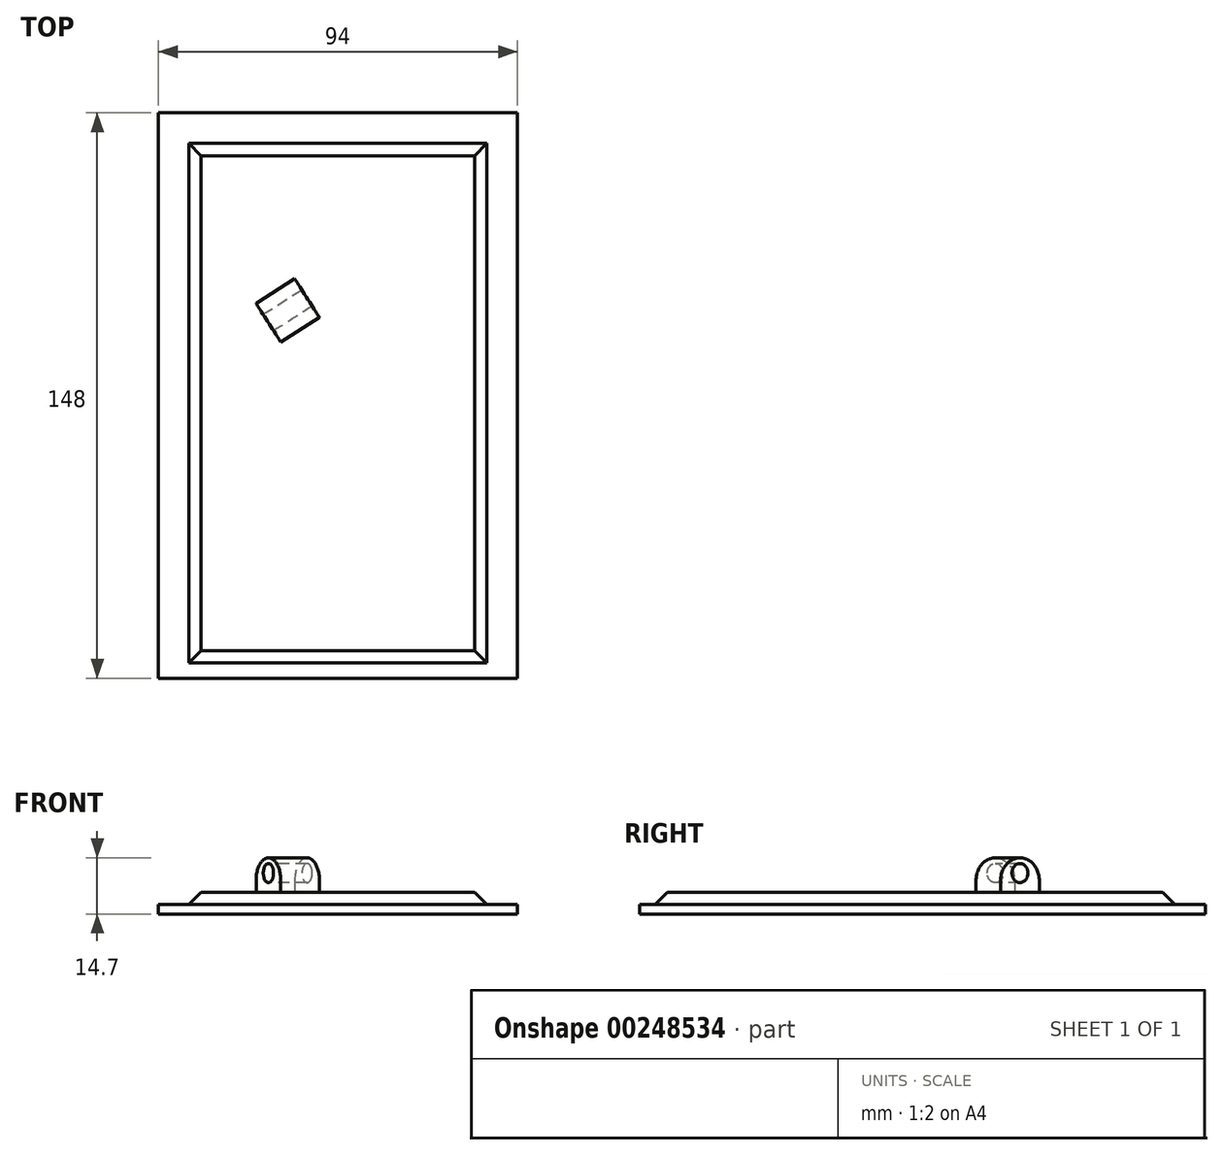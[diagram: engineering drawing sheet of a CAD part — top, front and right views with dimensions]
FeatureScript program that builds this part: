
annotation { "Feature Type Name" : "Feature", "Feature Type Description" : "" }
export const myFeature = defineFeature(function(context is Context, id is Id, definition is map)
    precondition{}
    {
        {
            var Q0;
            Q0=qCreatedBy(makeId("Top.planeOp"),FACE);
            var sketch = newSketch(context, id + "F0", { "sketchPlane" : qUnion([Q0])});
            skLineSegment(sketch, "E0.bottom", {"start": v(47, 74) * mm, "end": v(-47, 74) * mm});
            skLineSegment(sketch, "E0.top", {"start": v(47, -74) * mm, "end": v(-47, -74) * mm});
            skLineSegment(sketch, "E0.left", {"start": v(47, 74) * mm, "end": v(47, -74) * mm});
            skLineSegment(sketch, "E0.right", {"start": v(-47, 74) * mm, "end": v(-47, -74) * mm});
            skPoint(sketch, "E0.middle", {"position": v(0, 0) * mm});
            skLineSegment(sketch, "E1.left", {"start": v(47, -74) * mm, "end": v(47, 74) * mm});
            skLineSegment(sketch, "E1.right", {"start": v(-47, -74) * mm, "end": v(-47, 74) * mm});
            skLineSegment(sketch, "E2.bottom", {"start": v(-39, 66) * mm, "end": v(39, 66) * mm});
            skLineSegment(sketch, "E2.top", {"start": v(-39, -70) * mm, "end": v(39, -70) * mm});
            skLineSegment(sketch, "E2.left", {"start": v(-39, 66) * mm, "end": v(-39, -70) * mm});
            skLineSegment(sketch, "E2.right", {"start": v(39, 66) * mm, "end": v(39, -70) * mm});
            skSolve(sketch);
        }
        {
            var Q0;
            Q0=makeQuery(id+"F0.imprint","IMPRINT",FACE,{"disambiguationData":[TD([[makeQuery(id+"F0.imprint","IMPRINT",EDGE,{"derivedFrom":sQuery(id+"F0.wireOp",EDGE,"E0.bottom")}),-1.0]])]});
            var Q1;
            Q1=makeQuery(id+"F0.imprint","IMPRINT",FACE,{"disambiguationData":[TD([[makeQuery(id+"F0.imprint","IMPRINT",EDGE,{"derivedFrom":sQuery(id+"F0.wireOp",EDGE,"E0.bottom")}),1.0]])]});
            var Q2;
            Q2=makeQuery(id+"F0.imprint","IMPRINT",FACE,{"disambiguationData":[TD([[makeQuery(id+"F0.imprint","IMPRINT",EDGE,{"derivedFrom":sQuery(id+"F0.wireOp",EDGE,"E2.bottom")}),-1.0]])]});
            var Q3;
            Q3=makeQuery(id+"F0.imprint","IMPRINT",FACE,{"disambiguationData":[TD([[makeQuery(id+"F0.imprint","IMPRINT",EDGE,{"derivedFrom":sQuery(id+"F0.wireOp",EDGE,"E0.top")}),-1.0]])]});
            extrude(context, id + "F1", {"entities" : qUnion([Q0, Q1, Q2, Q3]), "oppositeDirection" : true, "depth" : 2.5 * mm});
        }
        {
            var Q0;
            Q0=makeQuery(id+"F0.imprint","IMPRINT",FACE,{"disambiguationData":[TD([[makeQuery(id+"F0.imprint","IMPRINT",EDGE,{"derivedFrom":sQuery(id+"F0.wireOp",EDGE,"E2.bottom")}),-1.0]])]});
            extrude(context, id + "F2", {"entities" : qUnion([Q0]), "operationType" : NewBodyOperationType.ADD, "depth" : 3.2 * mm});
        }
        {
            var Q0;
            Q0=makeQuery(id+"F2.opExtrude","CAP_EDGE",EDGE,{"disambiguationData":[OSD([sQuery(id+"F0.wireOp",EDGE,"E0.top")])],"isStart":false});
            var Q1;
            Q1=makeQuery(id+"F2.opExtrude","CAP_EDGE",EDGE,{"disambiguationData":[OSD([sQuery(id+"F0.wireOp",EDGE,"E0.right")])],"isStart":false});
            var Q2;
            Q2=makeQuery(id+"F2.opExtrude","CAP_EDGE",EDGE,{"disambiguationData":[OSD([sQuery(id+"F0.wireOp",EDGE,"E0.left")])],"isStart":false});
            var Q3;
            Q3=makeQuery(id+"F2.opExtrude","CAP_EDGE",EDGE,{"disambiguationData":[OSD([sQuery(id+"F0.wireOp",EDGE,"E0.bottom")])],"isStart":false});
            var Q4;
            Q4=makeQuery(id+"F2.opExtrude","CAP_EDGE",EDGE,{"disambiguationData":[OSD([sQuery(id+"F0.wireOp",EDGE,"E2.left")])],"isStart":false});
            var Q5;
            Q5=makeQuery(id+"F2.opExtrude","CAP_EDGE",EDGE,{"disambiguationData":[OSD([sQuery(id+"F0.wireOp",EDGE,"E2.top")])],"isStart":false});
            var Q6;
            Q6=makeQuery(id+"F2.opExtrude","CAP_EDGE",EDGE,{"disambiguationData":[OSD([sQuery(id+"F0.wireOp",EDGE,"E2.right")])],"isStart":false});
            var Q7;
            Q7=makeQuery(id+"F2.opExtrude","CAP_EDGE",EDGE,{"disambiguationData":[OSD([sQuery(id+"F0.wireOp",EDGE,"E2.bottom")])],"isStart":false});
            chamfer(context, id + "F3", {"entities" : qUnion([Q0, Q1, Q2, Q3, Q4, Q5, Q6, Q7]), "width" : 3.2 * mm, "tangentPropagation" : true});
        }
        {
            var Q0;
            Q0=makeQuery(id+"F2.opExtrude","CAP_FACE",FACE,{"disambiguationData":[OSD([sQuery(id+"F0.wireOp",EDGE,"E2.bottom"),sQuery(id+"F0.wireOp",EDGE,"E2.top"),sQuery(id+"F0.wireOp",EDGE,"E2.left"),sQuery(id+"F0.wireOp",EDGE,"E2.right")])],"isStart":false});
            var sketch = newSketch(context, id + "F4", { "sketchPlane" : qUnion([Q0])});
            skLineSegment(sketch, "E3.bottom", {"start": v(-43.3, 70.8) * mm, "end": v(42.3, 70.8) * mm, "construction": true});
            skLineSegment(sketch, "E3.top", {"start": v(-43.3, -67.2) * mm, "end": v(42.3, -67.2) * mm, "construction": true});
            skLineSegment(sketch, "E3.left", {"start": v(-43.3, 70.8) * mm, "end": v(-43.3, -67.2) * mm, "construction": true});
            skLineSegment(sketch, "E3.right", {"start": v(42.3, 70.8) * mm, "end": v(42.3, -67.2) * mm, "construction": true});
            skLineSegment(sketch, "E4", {"start": v(-0.5, 70.8) * mm, "end": v(-0.5, -67.2) * mm});
            skLineSegment(sketch, "E5", {"start": v(-43.3, 24.8) * mm, "end": v(42.3, 24.8) * mm, "construction": true});
            skLineSegment(sketch, "E6", {"start": v(-14.77, 83.2) * mm, "end": v(-14.77, -67.2) * mm, "construction": true});
            skPoint(sketch, "E7.0", {"position": v(-50.1, 77.6) * mm});
            skPoint(sketch, "E8.0", {"position": v(49.1, -74) * mm});
            skLineSegment(sketch, "E9.bottom", {"start": v(-50.1, 77.6) * mm, "end": v(49.1, 77.6) * mm, "construction": true});
            skLineSegment(sketch, "E9.top", {"start": v(-50.1, -74) * mm, "end": v(49.1, -74) * mm, "construction": true});
            skLineSegment(sketch, "E9.left", {"start": v(-50.1, 77.6) * mm, "end": v(-50.1, -74) * mm, "construction": true});
            skLineSegment(sketch, "E9.right", {"start": v(49.1, 77.6) * mm, "end": v(49.1, -74) * mm, "construction": true});
            skLineSegment(sketch, "E10.bottom", {"start": v(55.5, 81) * mm, "end": v(-56.5, 81) * mm, "construction": true});
            skLineSegment(sketch, "E10.top", {"start": v(55.5, -74) * mm, "end": v(-56.5, -74) * mm, "construction": true});
            skLineSegment(sketch, "E10.left", {"start": v(55.5, 81) * mm, "end": v(55.5, -74) * mm, "construction": true});
            skLineSegment(sketch, "E10.right", {"start": v(-56.5, 81) * mm, "end": v(-56.5, -74) * mm, "construction": true});
            skPoint(sketch, "E10.middle", {"position": v(-0.5, 3.5) * mm});
            skLineSegment(sketch, "E11.bottom", {"start": v(55.5, -74) * mm, "end": v(35.5, -74) * mm, "construction": true});
            skLineSegment(sketch, "E11.top", {"start": v(55.5, -54) * mm, "end": v(35.5, -54) * mm, "construction": true});
            skLineSegment(sketch, "E11.left", {"start": v(55.5, -74) * mm, "end": v(55.5, -54) * mm, "construction": true});
            skLineSegment(sketch, "E11.right", {"start": v(35.5, -74) * mm, "end": v(35.5, -54) * mm, "construction": true});
            skArc(sketch, "E12", {"start": v(35.5, -74) * mm, "mid": v(49.64, -68.14) * mm, "end": v(55.5, -54) * mm});
            skLineSegment(sketch, "E13.bottom", {"start": v(55.5, -74) * mm, "end": v(4.15, -74) * mm, "construction": true});
            skLineSegment(sketch, "E13.top", {"start": v(55.5, -34) * mm, "end": v(15.5, -34) * mm, "construction": true});
            skLineSegment(sketch, "E13.left", {"start": v(55.5, -74) * mm, "end": v(55.5, -34) * mm, "construction": true});
            skLineSegment(sketch, "E13.right", {"start": v(15.5, -61.6) * mm, "end": v(15.5, -34) * mm, "construction": true});
            skLineSegment(sketch, "E14", {"start": v(4.15, -74) * mm, "end": v(55.5, -41.24) * mm, "construction": true});
            skArc(sketch, "E15", {"start": v(35.5, -74) * mm, "mid": v(25.89, -71.54) * mm, "end": v(18.64, -64.76) * mm});
            skArc(sketch, "E16", {"start": v(55.5, -54) * mm, "mid": v(54.7, -48.4) * mm, "end": v(52.36, -43.24) * mm});
            skLineSegment(sketch, "E17", {"start": v(35.5, -54) * mm, "end": v(-14.77, 24.8) * mm, "construction": true});
            skLineSegment(sketch, "E18", {"start": v(-4.01, 7.94) * mm, "end": v(-12.44, 2.56) * mm, "construction": true});
            skLineSegment(sketch, "E19", {"start": v(-12.44, 2.56) * mm, "end": v(4.42, 13.32) * mm, "construction": true});
            skFitSpline(sketch, "E20", {"points": [v(18.64, -64.76) * mm, v(-12.44, 2.56) * mm], "startDerivative": vector(-25.68, 50.47) * mm, "endDerivative": vector(-40.94, 31.95) * mm});
            skLineSegment(sketch, "E21", {"start": v(1.2, -8.09) * mm, "end": v(4.76, -5.82) * mm, "construction": true});
            skLineSegment(sketch, "E22", {"start": v(4.76, -5.82) * mm, "end": v(8.33, -3.55) * mm, "construction": true});
            skLineSegment(sketch, "E23", {"start": v(10.08, -47.93) * mm, "end": v(25.4, -38.16) * mm, "construction": true});
            skLineSegment(sketch, "E24", {"start": v(25.4, -38.16) * mm, "end": v(40.71, -28.4) * mm, "construction": true});
            skFitSpline(sketch, "E25", {"points": [v(52.36, -43.24) * mm, v(4.42, 13.32) * mm], "startDerivative": vector(-34.95, 44.56) * mm, "endDerivative": vector(-11.72, 50.59) * mm});
            skLineSegment(sketch, "E26", {"start": v(-14.77, 24.8) * mm, "end": v(-27.41, 16.73) * mm, "construction": true});
            skLineSegment(sketch, "E27", {"start": v(-14.77, 24.8) * mm, "end": v(-2.12, 32.87) * mm, "construction": true});
            skFitSpline(sketch, "E28", {"points": [v(-12.44, 2.56) * mm, v(-27.41, 16.73) * mm], "startDerivative": vector(-21.07, 20.86) * mm, "endDerivative": vector(-15, 27.3) * mm});
            skFitSpline(sketch, "E29", {"points": [v(4.42, 13.32) * mm, v(-2.12, 32.87) * mm], "startDerivative": vector(-10.03, 27.9) * mm, "endDerivative": vector(-19.18, 26.47) * mm});
            skLineSegment(sketch, "E30", {"start": v(-22.41, 7.63) * mm, "end": v(-19.46, 9.51) * mm, "construction": true});
            skLineSegment(sketch, "E31", {"start": v(-19.46, 9.51) * mm, "end": v(-9.2, 16.06) * mm, "construction": true});
            skLineSegment(sketch, "E32", {"start": v(-9.2, 16.06) * mm, "end": v(4.22, 24.04) * mm, "construction": true});
            skLineSegment(sketch, "E33", {"start": v(-14.77, 24.8) * mm, "end": v(-20.14, 33.23) * mm, "construction": true});
            skLineSegment(sketch, "E34", {"start": v(-27.41, 16.73) * mm, "end": v(-30.1, 20.95) * mm});
            skLineSegment(sketch, "E35", {"start": v(-28.58, 27.85) * mm, "end": v(-20.14, 33.23) * mm});
            skLineSegment(sketch, "E36", {"start": v(-2.12, 32.87) * mm, "end": v(-4.8, 37.08) * mm});
            skLineSegment(sketch, "E37", {"start": v(-11.71, 38.6) * mm, "end": v(-20.14, 33.23) * mm});
            skPoint(sketch, "E38.visualSharp", {"position": v(-32.8, 25.16) * mm});
            skArc(sketch, "E38.filletArc", {"start": v(-28.58, 27.85) * mm, "mid": v(-30.77, 24.72) * mm, "end": v(-30.1, 20.95) * mm});
            skPoint(sketch, "E39.visualSharp", {"position": v(-7.5, 41.3) * mm});
            skArc(sketch, "E39.filletArc", {"start": v(-4.8, 37.08) * mm, "mid": v(-7.95, 39.28) * mm, "end": v(-11.71, 38.6) * mm});
            skSolve(sketch);
        }
        {
            var Q0;
            Q0=makeQuery(id+"F2.opExtrude","CAP_FACE",FACE,{"disambiguationData":[OSD([sQuery(id+"F0.wireOp",EDGE,"E2.bottom"),sQuery(id+"F0.wireOp",EDGE,"E2.top"),sQuery(id+"F0.wireOp",EDGE,"E2.left"),sQuery(id+"F0.wireOp",EDGE,"E2.right")])],"isStart":false});
            var sketch = newSketch(context, id + "F5", { "sketchPlane" : qUnion([Q0])});
            skPoint(sketch, "E40.0", {"position": v(-14.77, 24.8) * mm});
            skPoint(sketch, "E41.0", {"position": v(-27.41, 16.73) * mm});
            skPoint(sketch, "E42.0", {"position": v(-2.12, 32.87) * mm});
            skLineSegment(sketch, "E43", {"start": v(-27.41, 16.73) * mm, "end": v(-2.12, 32.87) * mm, "construction": true});
            skLineSegment(sketch, "E44", {"start": v(-19.83, 21.57) * mm, "end": v(-21.44, 24.1) * mm});
            skLineSegment(sketch, "E45", {"start": v(-19.83, 21.57) * mm, "end": v(-14.98, 13.99) * mm});
            skLineSegment(sketch, "E46", {"start": v(-14.98, 13.99) * mm, "end": v(-4.87, 20.44) * mm});
            skLineSegment(sketch, "E47", {"start": v(-4.87, 20.44) * mm, "end": v(-11.32, 30.56) * mm});
            skLineSegment(sketch, "E48", {"start": v(-11.32, 30.56) * mm, "end": v(-21.44, 24.1) * mm});
            skSolve(sketch);
        }
        {
            var Q0;
            Q0=makeQuery(id+"F5.imprint","IMPRINT",FACE,{"disambiguationData":[TD([[makeQuery(id+"F5.imprint","IMPRINT",EDGE,{"derivedFrom":sQuery(id+"F5.wireOp",EDGE,"E44")}),-1.0]])]});
            extrude(context, id + "F6", {"entities" : qUnion([Q0]), "operationType" : NewBodyOperationType.ADD, "depth" : 9 * mm});
        }
        {
            var Q0;
            Q0=makeQuery(id+"F6.opExtrude","CAP_EDGE",EDGE,{"disambiguationData":[OSD([sQuery(id+"F5.wireOp",EDGE,"E46")])],"isStart":false});
            var Q1;
            Q1=makeQuery(id+"F6.opExtrude","CAP_EDGE",EDGE,{"disambiguationData":[OSD([sQuery(id+"F5.wireOp",EDGE,"E48")])],"isStart":false});
            fillet(context, id + "F7", {"entities" : qUnion([Q0, Q1]), "radius" : 6 * mm, "tangentPropagation" : true, "allowEdgeOverflow" : false});
        }
        {
            var Q0;
            Q0=makeQuery(id+"F6.opExtrude","SWEPT_FACE",FACE,{"disambiguationData":[OSD([sQuery(id+"F5.wireOp",EDGE,"E44"),sQuery(id+"F5.wireOp",EDGE,"E45")])]});
            var sketch = newSketch(context, id + "F8", { "sketchPlane" : qUnion([Q0])});
            skLineSegment(sketch, "E49", {"start": v(-31.85, 6.2) * mm, "end": v(-19.85, 6.2) * mm, "construction": true});
            skLineSegment(sketch, "E50", {"start": v(-19.85, 6.2) * mm, "end": v(-25.85, 6.2) * mm, "construction": true});
            skLineSegment(sketch, "E51", {"start": v(-25.85, 12.2) * mm, "end": v(-25.85, 6.2) * mm, "construction": true});
            skCircle(sketch, "E52", {"center": v(-25.85, 8.2) * mm, "radius": 2.5 * mm});
            skSolve(sketch);
        }
        {
            var Q0;
            Q0=makeQuery(id+"F8.imprint","IMPRINT",FACE,{"disambiguationData":[TD([[makeQuery(id+"F8.imprint","IMPRINT",EDGE,{"derivedFrom":sQuery(id+"F8.wireOp",EDGE,"E52")}),1.0]])]});
            extrude(context, id + "F9", {"entities" : qUnion([Q0]), "operationType" : NewBodyOperationType.REMOVE, "oppositeDirection" : true, "depth" : 12.1 * mm});
        }
    });
